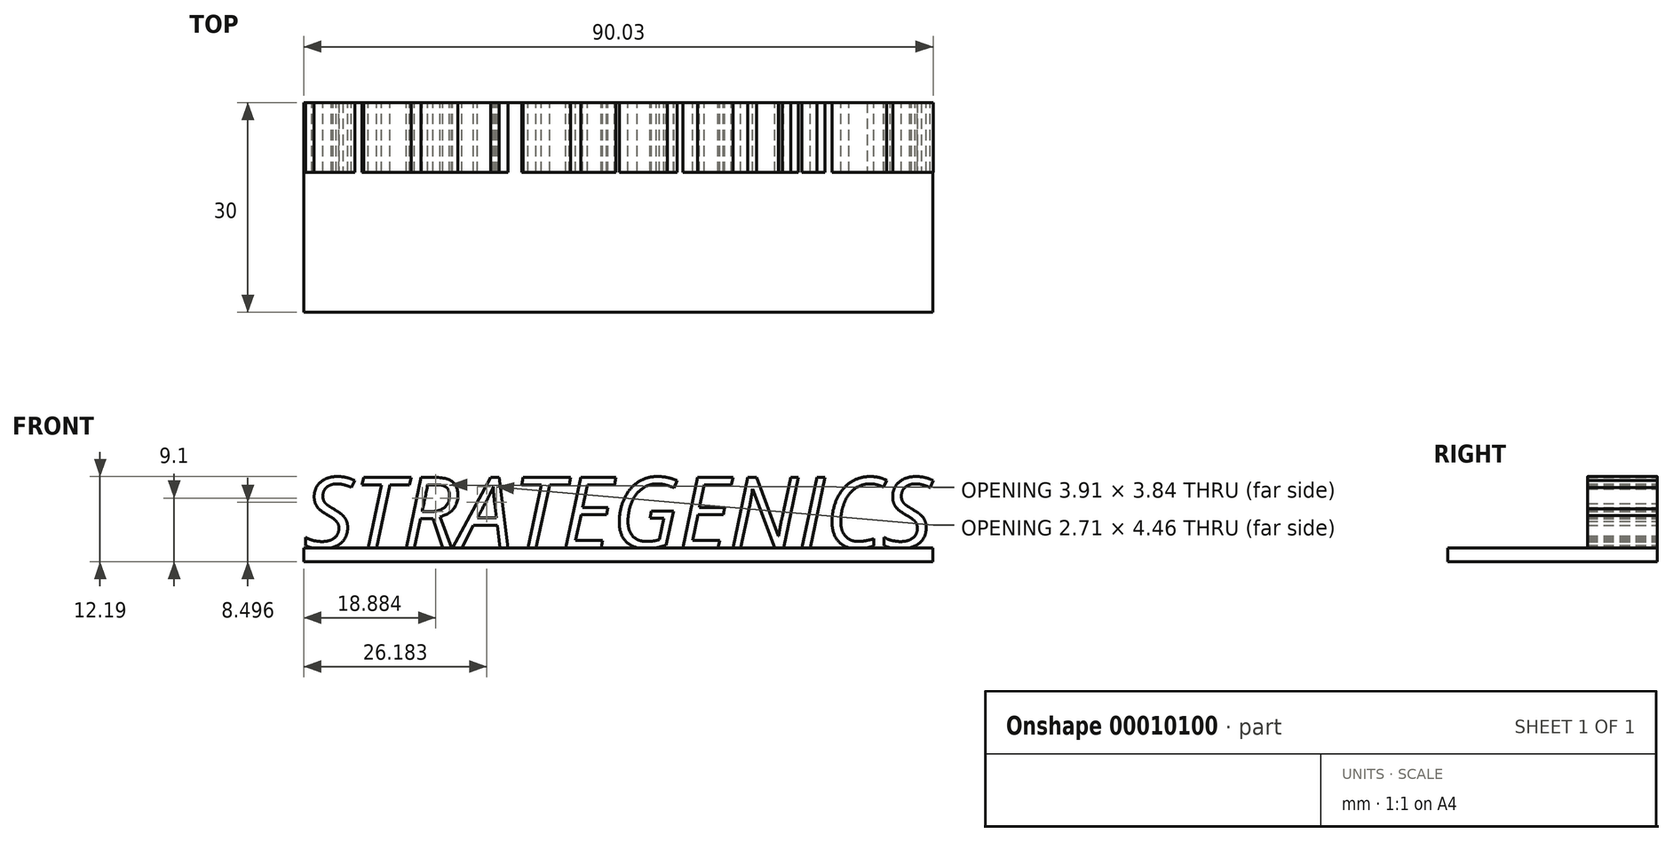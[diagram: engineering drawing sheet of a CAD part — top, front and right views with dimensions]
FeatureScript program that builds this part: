
annotation { "Feature Type Name" : "Feature", "Feature Type Description" : "" }
export const myFeature = defineFeature(function(context is Context, id is Id, definition is map)
    precondition{}
    {
        {
            var Q0;
            Q0=qCreatedBy(makeId("Top.planeOp"),FACE);
            var sketch = newSketch(context, id + "F0", { "sketchPlane" : qUnion([Q0])});
            skLineSegment(sketch, "E0.bottom", {"start": v(0, 0) * mm, "end": v(90, 0) * mm});
            skLineSegment(sketch, "E0.top", {"start": v(0, -30) * mm, "end": v(90, -30) * mm});
            skLineSegment(sketch, "E0.left", {"start": v(0, 0) * mm, "end": v(0, -30) * mm});
            skLineSegment(sketch, "E0.right", {"start": v(90, 0) * mm, "end": v(90, -30) * mm});
            skSolve(sketch);
        }
        {
            var Q0;
            Q0=makeQuery(id+"F0.imprint","IMPRINT",FACE,{"disambiguationData":[TD([[makeQuery(id+"F0.imprint","IMPRINT",EDGE,{"derivedFrom":sQuery(id+"F0.wireOp",EDGE,"E0.bottom")}),-1.0]])]});
            extrude(context, id + "F1", {"entities" : qUnion([Q0]), "depth" : 2 * mm});
        }
        {
            var Q0;
            Q0=qCreatedBy(makeId("Front.planeOp"),FACE);
            var sketch = newSketch(context, id + "F2", { "sketchPlane" : qUnion([Q0])});
            skText(sketch, "E1", { "text": "STRATEGENICS", "fontName": "OpenSans-Italic.ttf"});
            skPoint(sketch, "E2.0", {"position": v(0, 2) * mm});
            const initialGuessF2  = {"E1": [0, 0.002, 1, 0, 0.01013]};
            skSetInitialGuess(sketch, initialGuessF2);
            skSolve(sketch);
        }
        {
            var Q0;
            Q0=makeQuery(id+"F2.imprint","IMPRINT",FACE,{"disambiguationData":[TD([[makeQuery(id+"F2.imprint","IMPRINT",EDGE,{"derivedFrom":sQuery(id+"F2.wireOp",EDGE,"E1.sketch_text.stroke-0")}),-1.0]])]});
            var Q1;
            Q1=makeQuery(id+"F2.imprint","IMPRINT",FACE,{"disambiguationData":[TD([[makeQuery(id+"F2.imprint","IMPRINT",EDGE,{"derivedFrom":sQuery(id+"F2.wireOp",EDGE,"E1.sketch_text.stroke-27")}),-1.0]])]});
            var Q2;
            Q2=makeQuery(id+"F2.imprint","IMPRINT",FACE,{"disambiguationData":[TD([[makeQuery(id+"F2.imprint","IMPRINT",EDGE,{"derivedFrom":sQuery(id+"F2.wireOp",EDGE,"E1.sketch_text.stroke-35")}),-1.0]])]});
            var Q3;
            Q3=makeQuery(id+"F2.imprint","IMPRINT",FACE,{"disambiguationData":[TD([[makeQuery(id+"F2.imprint","IMPRINT",EDGE,{"derivedFrom":sQuery(id+"F2.wireOp",EDGE,"E1.sketch_text.stroke-52")}),-1.0]])]});
            var Q4;
            Q4=makeQuery(id+"F2.imprint","IMPRINT",FACE,{"disambiguationData":[TD([[makeQuery(id+"F2.imprint","IMPRINT",EDGE,{"derivedFrom":sQuery(id+"F2.wireOp",EDGE,"E1.sketch_text.stroke-65")}),-1.0]])]});
            var Q5;
            Q5=makeQuery(id+"F2.imprint","IMPRINT",FACE,{"disambiguationData":[TD([[makeQuery(id+"F2.imprint","IMPRINT",EDGE,{"derivedFrom":sQuery(id+"F2.wireOp",EDGE,"E1.sketch_text.stroke-73")}),-1.0]])]});
            var Q6;
            Q6=makeQuery(id+"F2.imprint","IMPRINT",FACE,{"disambiguationData":[TD([[makeQuery(id+"F2.imprint","IMPRINT",EDGE,{"derivedFrom":sQuery(id+"F2.wireOp",EDGE,"E1.sketch_text.stroke-85")}),-1.0]])]});
            var Q7;
            Q7=makeQuery(id+"F2.imprint","IMPRINT",FACE,{"disambiguationData":[TD([[makeQuery(id+"F2.imprint","IMPRINT",EDGE,{"derivedFrom":sQuery(id+"F2.wireOp",EDGE,"E1.sketch_text.stroke-107")}),-1.0]])]});
            var Q8;
            Q8=makeQuery(id+"F2.imprint","IMPRINT",FACE,{"disambiguationData":[TD([[makeQuery(id+"F2.imprint","IMPRINT",EDGE,{"derivedFrom":sQuery(id+"F2.wireOp",EDGE,"E1.sketch_text.stroke-119")}),-1.0]])]});
            var Q9;
            Q9=makeQuery(id+"F2.imprint","IMPRINT",FACE,{"disambiguationData":[TD([[makeQuery(id+"F2.imprint","IMPRINT",EDGE,{"derivedFrom":sQuery(id+"F2.wireOp",EDGE,"E1.sketch_text.stroke-133")}),-1.0]])]});
            var Q10;
            Q10=makeQuery(id+"F2.imprint","IMPRINT",FACE,{"disambiguationData":[TD([[makeQuery(id+"F2.imprint","IMPRINT",EDGE,{"derivedFrom":sQuery(id+"F2.wireOp",EDGE,"E1.sketch_text.stroke-137")}),-1.0]])]});
            var Q11;
            Q11=makeQuery(id+"F2.imprint","IMPRINT",FACE,{"disambiguationData":[TD([[makeQuery(id+"F2.imprint","IMPRINT",EDGE,{"derivedFrom":sQuery(id+"F2.wireOp",EDGE,"E1.sketch_text.stroke-154")}),-1.0]])]});
            extrude(context, id + "F3", {"entities" : qUnion([Q0, Q1, Q2, Q3, Q4, Q5, Q6, Q7, Q8, Q9, Q10, Q11]), "operationType" : NewBodyOperationType.ADD, "depth" : 10 * mm});
        }
    });
